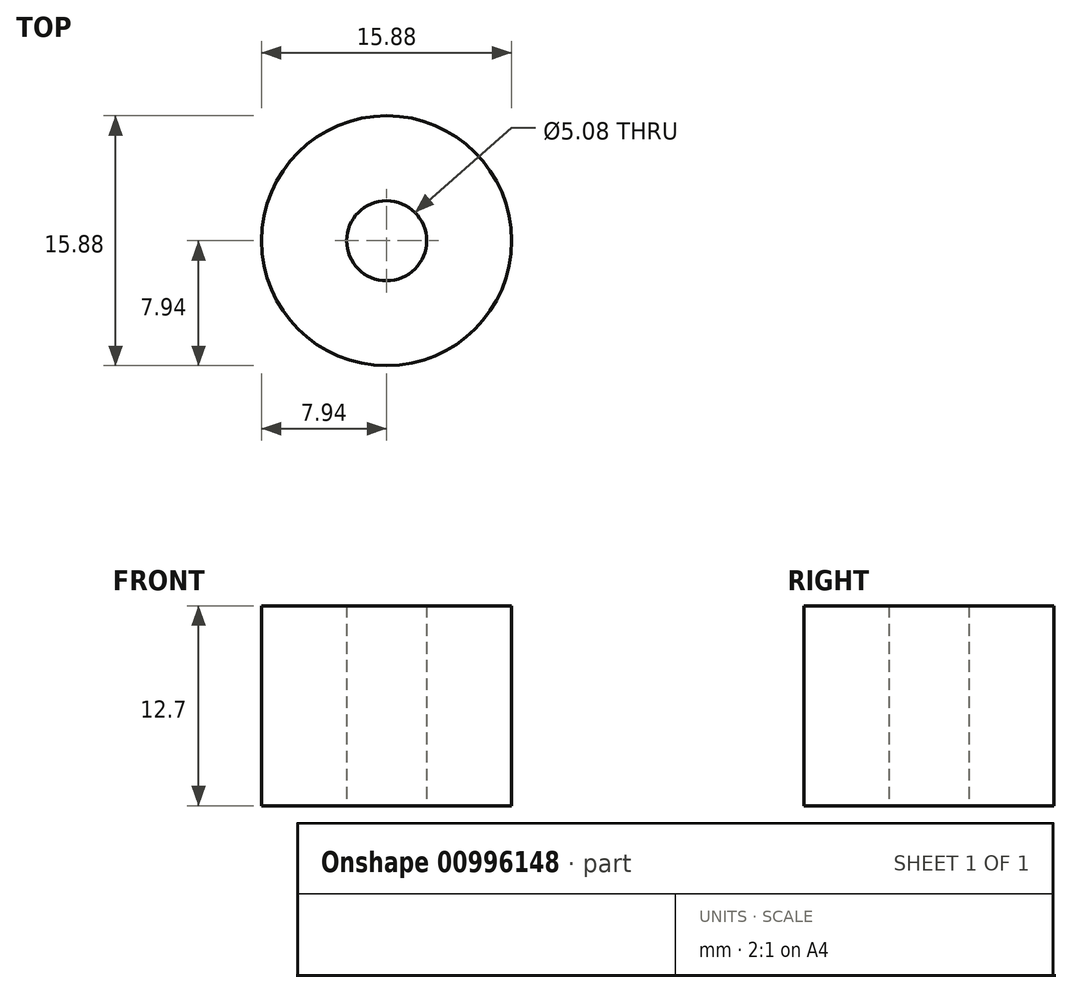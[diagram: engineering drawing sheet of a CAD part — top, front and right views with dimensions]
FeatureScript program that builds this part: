
annotation { "Feature Type Name" : "Feature", "Feature Type Description" : "" }
export const myFeature = defineFeature(function(context is Context, id is Id, definition is map)
    precondition{}
    {
        {
            var Q0;
            Q0=qCreatedBy(makeId("Top.planeOp"),FACE);
            var sketch = newSketch(context, id + "F0", { "sketchPlane" : qUnion([Q0])});
            skCircle(sketch, "E0", {"center": v(0, 0) * mm, "radius": 7.94 * mm});
            skCircle(sketch, "E1", {"center": v(0, 0) * mm, "radius": 2.54 * mm});
            skSolve(sketch);
        }
        {
            var Q0;
            Q0=makeQuery(id+"F0.imprint","IMPRINT",FACE,{"disambiguationData":[TD([[makeQuery(id+"F0.imprint","IMPRINT",EDGE,{"derivedFrom":sQuery(id+"F0.wireOp",EDGE,"E0")}),1.0]])]});
            extrude(context, id + "F1", {"entities" : qUnion([Q0]), "depth" : 12.7 * mm, "offsetDistance" : 25.4 * mm});
        }
    });
